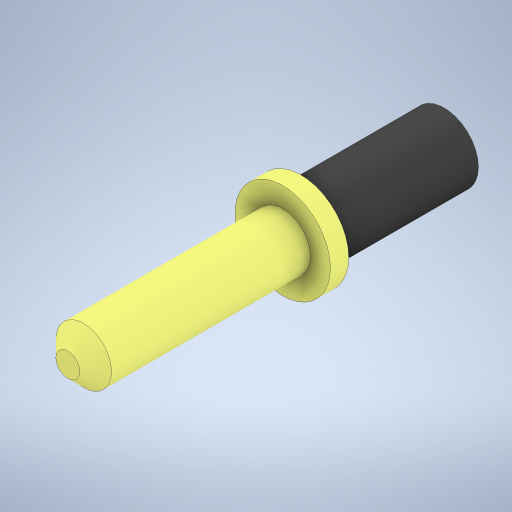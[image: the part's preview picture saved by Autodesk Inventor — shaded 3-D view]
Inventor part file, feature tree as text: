
AUTODESK INVENTOR PART (.ipt)
format: ipt  version: 2023.1 (Build 271208000, 208)  size: 261,120 bytes
history: native  units: mm
features: extrude x3, other x1, sketch x1, chamfer x1
ambient origin geometry x8: Origin, YZ Plane, XZ Plane, XY Plane, X Axis, Y Axis, Z Axis, Center Point
bodies: Body1 (feature_tree)
feature tree (6):
  other  "솔리드1"
  sketch  "스케치1"
  extrude  "돌출1"  Depth=3.5mm
  extrude  "돌출2"  Depth=6.0mm
  extrude  "돌출3"  Depth=4.3mm
  chamfer  "모따기1"  Distance=13.5mm
